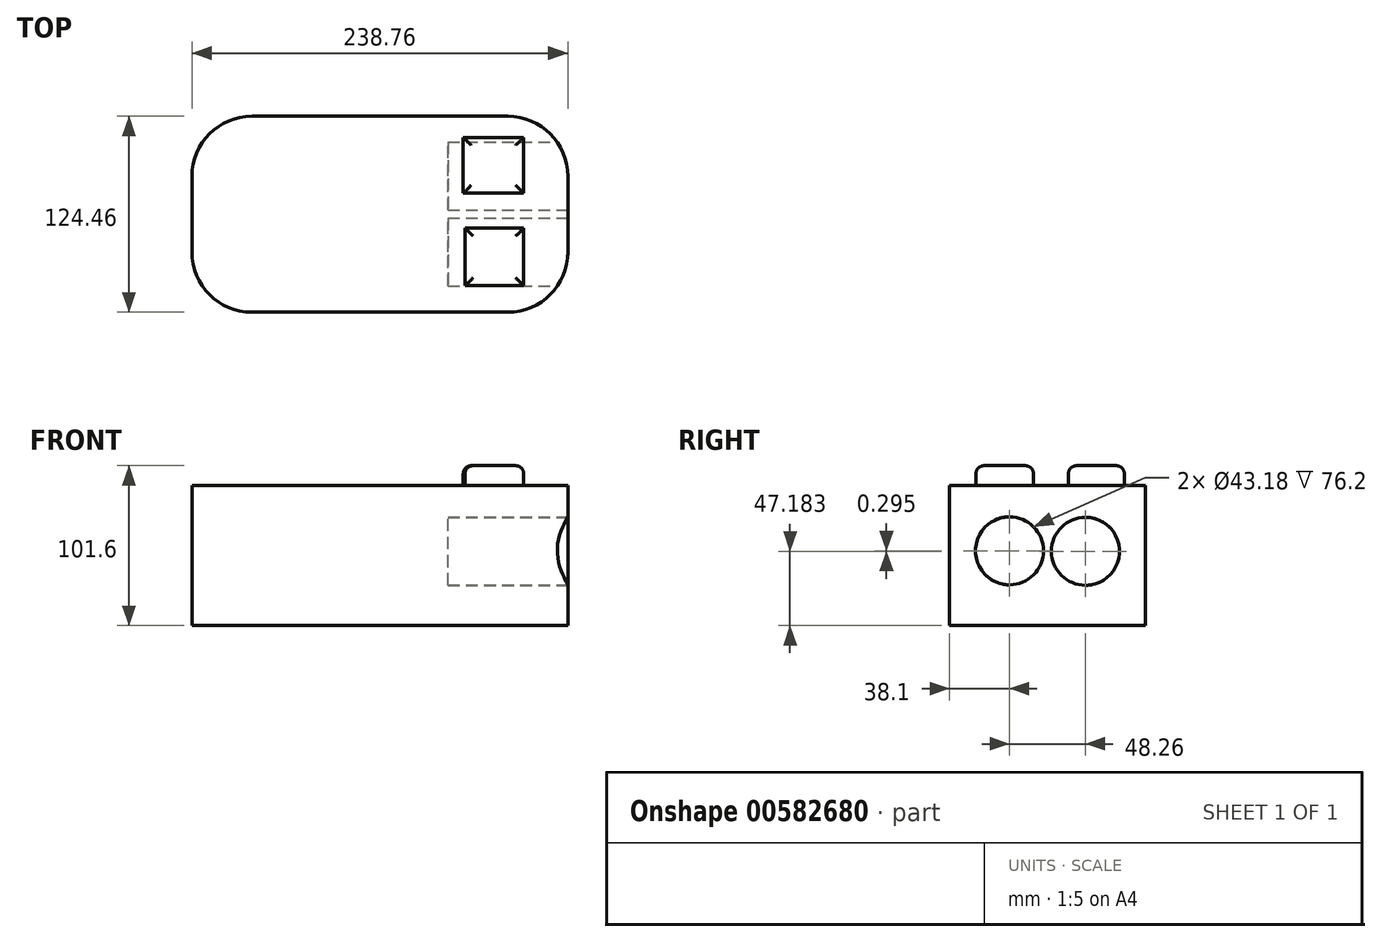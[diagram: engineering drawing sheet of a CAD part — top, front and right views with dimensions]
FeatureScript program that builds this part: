
annotation { "Feature Type Name" : "Feature", "Feature Type Description" : "" }
export const myFeature = defineFeature(function(context is Context, id is Id, definition is map)
    precondition{}
    {
        {
            var Q0;
            Q0=qCreatedBy(makeId("Top.planeOp"),FACE);
            var sketch = newSketch(context, id + "F0", { "sketchPlane" : qUnion([Q0])});
            skLineSegment(sketch, "E0", {"start": v(-37.68, 0) * mm, "end": v(124.88, 0) * mm});
            skLineSegment(sketch, "E1", {"start": v(162.98, 38.1) * mm, "end": v(162.98, 86.36) * mm});
            skLineSegment(sketch, "E2", {"start": v(124.88, 124.46) * mm, "end": v(-37.68, 124.46) * mm});
            skLineSegment(sketch, "E3", {"start": v(-75.78, 86.36) * mm, "end": v(-75.78, 38.1) * mm});
            skPoint(sketch, "E4.visualSharp", {"position": v(-75.78, 124.46) * mm});
            skArc(sketch, "E4.filletArc", {"start": v(-37.68, 124.46) * mm, "mid": v(-64.62, 113.3) * mm, "end": v(-75.78, 86.36) * mm});
            skPoint(sketch, "E5.visualSharp", {"position": v(-75.78, 0) * mm});
            skArc(sketch, "E5.filletArc", {"start": v(-75.78, 38.1) * mm, "mid": v(-64.62, 11.16) * mm, "end": v(-37.68, 0) * mm});
            skPoint(sketch, "E6.visualSharp", {"position": v(162.98, 0) * mm});
            skArc(sketch, "E6.filletArc", {"start": v(124.88, 0) * mm, "mid": v(151.82, 11.16) * mm, "end": v(162.98, 38.1) * mm});
            skPoint(sketch, "E7.visualSharp", {"position": v(162.98, 124.46) * mm});
            skArc(sketch, "E7.filletArc", {"start": v(162.98, 86.36) * mm, "mid": v(151.82, 113.3) * mm, "end": v(124.88, 124.46) * mm});
            skSolve(sketch);
        }
        {
            var Q0;
            Q0 = qSketchRegion(id + "F0", true);
            extrude(context, id + "F1", {"entities" : qUnion([Q0]), "depth" : 88.9 * mm, "offsetDistance" : 25.4 * mm});
        }
        {
            var Q0;
            Q0=makeQuery(id+"F1.opExtrude","SWEPT_FACE",FACE,{"disambiguationData":[OSD([sQuery(id+"F0.wireOp",EDGE,"E1")])]});
            var sketch = newSketch(context, id + "F2", { "sketchPlane" : qUnion([Q0])});
            skCircle(sketch, "E8", {"center": v(38.1, 47.48) * mm, "radius": 21.59 * mm});
            skCircle(sketch, "E9", {"center": v(86.36, 47.18) * mm, "radius": 21.59 * mm});
            skSolve(sketch);
        }
        {
            var Q0;
            Q0 = qSketchRegion(id + "F2", true);
            extrude(context, id + "F3", {"entities" : qUnion([Q0]), "operationType" : NewBodyOperationType.REMOVE, "oppositeDirection" : true, "depth" : 76.2 * mm, "offsetDistance" : 25.4 * mm});
        }
        {
            var Q0;
            Q0=makeQuery(id+"F1.opExtrude","CAP_FACE",FACE,{"disambiguationData":[OSD([sQuery(id+"F0.wireOp",EDGE,"E0"),sQuery(id+"F0.wireOp",EDGE,"E1"),sQuery(id+"F0.wireOp",EDGE,"E2"),sQuery(id+"F0.wireOp",EDGE,"E3"),sQuery(id+"F0.wireOp",EDGE,"E4.filletArc"),sQuery(id+"F0.wireOp",EDGE,"E5.filletArc"),sQuery(id+"F0.wireOp",EDGE,"E6.filletArc"),sQuery(id+"F0.wireOp",EDGE,"E7.filletArc")])],"isStart":false});
            var sketch = newSketch(context, id + "F4", { "sketchPlane" : qUnion([Q0])});
            skLineSegment(sketch, "E10.bottom", {"start": v(96.6, 111.02) * mm, "end": v(134.94, 111.02) * mm});
            skLineSegment(sketch, "E10.top", {"start": v(96.6, 75.55) * mm, "end": v(134.94, 75.55) * mm});
            skLineSegment(sketch, "E10.left", {"start": v(96.6, 111.02) * mm, "end": v(96.6, 75.55) * mm});
            skLineSegment(sketch, "E10.right", {"start": v(134.94, 111.02) * mm, "end": v(134.94, 75.55) * mm});
            skLineSegment(sketch, "E11.bottom", {"start": v(97.68, 53.33) * mm, "end": v(134.94, 53.33) * mm});
            skLineSegment(sketch, "E11.top", {"start": v(97.68, 16.78) * mm, "end": v(134.94, 16.78) * mm});
            skLineSegment(sketch, "E11.left", {"start": v(97.68, 53.33) * mm, "end": v(97.68, 16.78) * mm});
            skLineSegment(sketch, "E11.right", {"start": v(134.94, 53.33) * mm, "end": v(134.94, 16.78) * mm});
            skSolve(sketch);
        }
        {
            var Q0;
            Q0 = qSketchRegion(id + "F4", true);
            extrude(context, id + "F5", {"entities" : qUnion([Q0]), "operationType" : NewBodyOperationType.ADD, "depth" : 12.7 * mm, "offsetDistance" : 25.4 * mm});
        }
        {
            var Q0;
            Q0=makeQuery(id+"F5.opExtrude","CAP_FACE",FACE,{"disambiguationData":[OSD([sQuery(id+"F4.wireOp",EDGE,"E10.bottom"),sQuery(id+"F4.wireOp",EDGE,"E10.top"),sQuery(id+"F4.wireOp",EDGE,"E10.left"),sQuery(id+"F4.wireOp",EDGE,"E10.right")])],"isStart":false});
            var Q1;
            Q1=makeQuery(id+"F5.opExtrude","CAP_FACE",FACE,{"disambiguationData":[OSD([sQuery(id+"F4.wireOp",EDGE,"E11.bottom"),sQuery(id+"F4.wireOp",EDGE,"E11.top"),sQuery(id+"F4.wireOp",EDGE,"E11.left"),sQuery(id+"F4.wireOp",EDGE,"E11.right")])],"isStart":false});
            fillet(context, id + "F6", {"entities" : qUnion([Q0, Q1]), "radius" : 5.08 * mm, "tangentPropagation" : true, "allowEdgeOverflow" : false});
        }
    });
